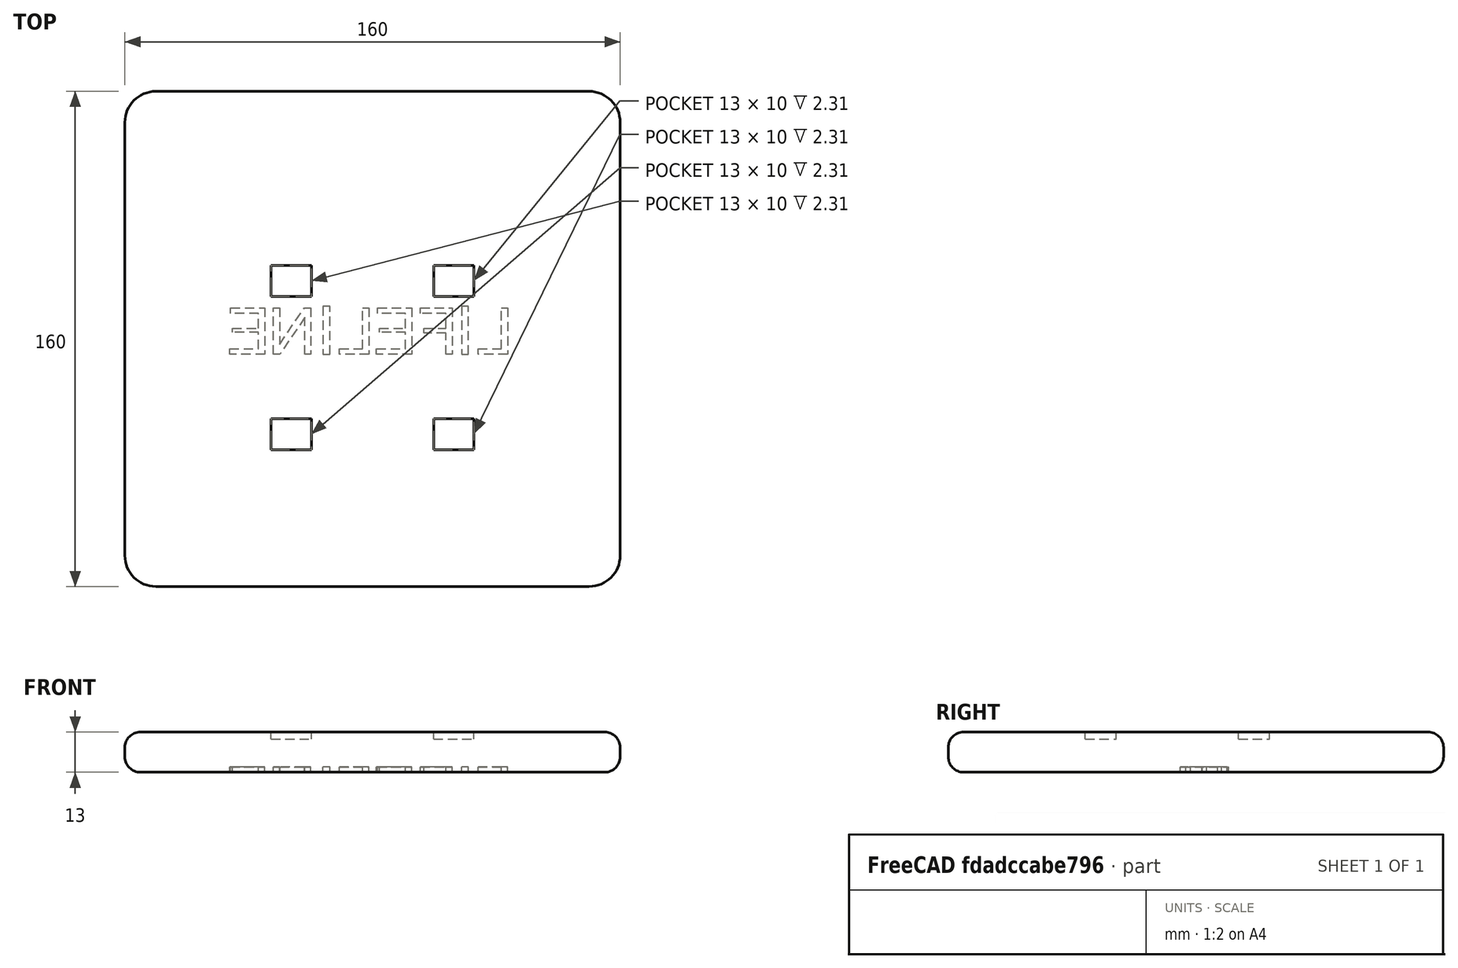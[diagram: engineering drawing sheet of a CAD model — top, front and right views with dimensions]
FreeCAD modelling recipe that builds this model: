
FCSTD DOCUMENT  (FreeCAD 0.17R13541 (Git))
Label: LifelineBody_Top
License: All rights reserved
LicenseURL: http://en.wikipedia.org/wiki/All_rights_reserved
objects: Part::Box×5, Part::Cut×5, Part::Fillet×3, Part::Part2DObjectPython×1, Part::FeaturePython×1, Part::Extrusion×1
note: 16 computed .brp shape members not serialized (recipe doc carries the construction recipe); baked Part::Feature solids carry a one-line shape summary decoded from their .brp

FEATURE [Part::Box] Box001  label="Base"
  AttacherType = Attacher::AttachEngine3D
  Height = 13
  Length = 160
  Width = 160
FEATURE [Part::Fillet] Fillet
  Base = -> Box001
  Edges = 4 edges r=10: [Edge1,Edge3,Edge5,Edge7]
FEATURE [Part::Fillet] Fillet001
  Base = -> Fillet
  Edges = 8 edges r=5: [Edge1,Edge5,Edge6,Edge7,Edge8,Edge9,Edge10,Edge11]
FEATURE [Part::Fillet] Fillet002
  Base = -> Fillet001
  Edges = 8 edges r=5: [Edge3,Edge6,Edge11,Edge12,Edge13,Edge14,Edge15,Edge16]
  Placement = pos=(-80,-80,-13) rot=(0,0,1;0rad)
FEATURE [Part::Box] Box  label="Cube"
  AttacherType = Attacher::AttachEngine3D
  Height = 2.31
  Length = 13
  Placement = pos=(19.75,13.75,-2.31) rot=(0,0,1;0rad)
  Width = 10
FEATURE [Part::Box] Box002  label="Cube001"
  AttacherType = Attacher::AttachEngine3D
  Height = 2.31
  Length = 13
  Placement = pos=(19.75,-35.75,-2.31) rot=(0,0,1;0rad)
  Width = 10
FEATURE [Part::Box] Box003  label="Cube002"
  AttacherType = Attacher::AttachEngine3D
  Height = 2.31
  Length = 13
  Placement = pos=(-32.75,-35.75,-2.31) rot=(0,0,1;0rad)
  Width = 10
FEATURE [Part::Box] Box004  label="Cube003"
  AttacherType = Attacher::AttachEngine3D
  Height = 2.31
  Length = 13
  Placement = pos=(-32.75,13.75,-2.31) rot=(0,0,1;0rad)
  Width = 10
FEATURE [Part::Cut] Cut
  Base = -> Fillet002
  Tool = -> Box004
FEATURE [Part::Cut] Cut001
  Base = -> Cut
  Tool = -> Box003
FEATURE [Part::Cut] Cut002
  Base = -> Cut001
  Tool = -> Box
FEATURE [Part::Cut] Cut003
  Base = -> Cut002
  Tool = -> Box002
FEATURE [Part::Part2DObjectPython] ShapeString  # Draft 2D object (typed FeaturePython)
  FontFile = <userpath>/Downloads/BACKRG__.TTF
  Placement = pos=(0,0,-13) rot=(0,0,1;0rad)
  Size = 1
  String = ENILEFIL
  Tracking = 0
FEATURE [Part::FeaturePython] Scale  # Draft clone (typed FeaturePython)
  Fuse = false
  Objects = -> [ShapeString]
  Placement = pos=(-47.5,0,-13.01) rot=(0,0,1;0rad)
  Scale = (7,7,7)
FEATURE [Part::Extrusion] Extrude
  Base = -> Scale
  Dir = (0,0,1)
  DirMode = 2
  FaceMakerClass = Part::FaceMakerBullseye
  LengthFwd = 10
  LengthRev = 0
  Placement = pos=(0,-5,-8.25) rot=(0,0,1;0rad)
  Solid = false
  Symmetric = false
FEATURE [Part::Cut] Cut004
  Base = -> Cut003
  Tool = -> Extrude
